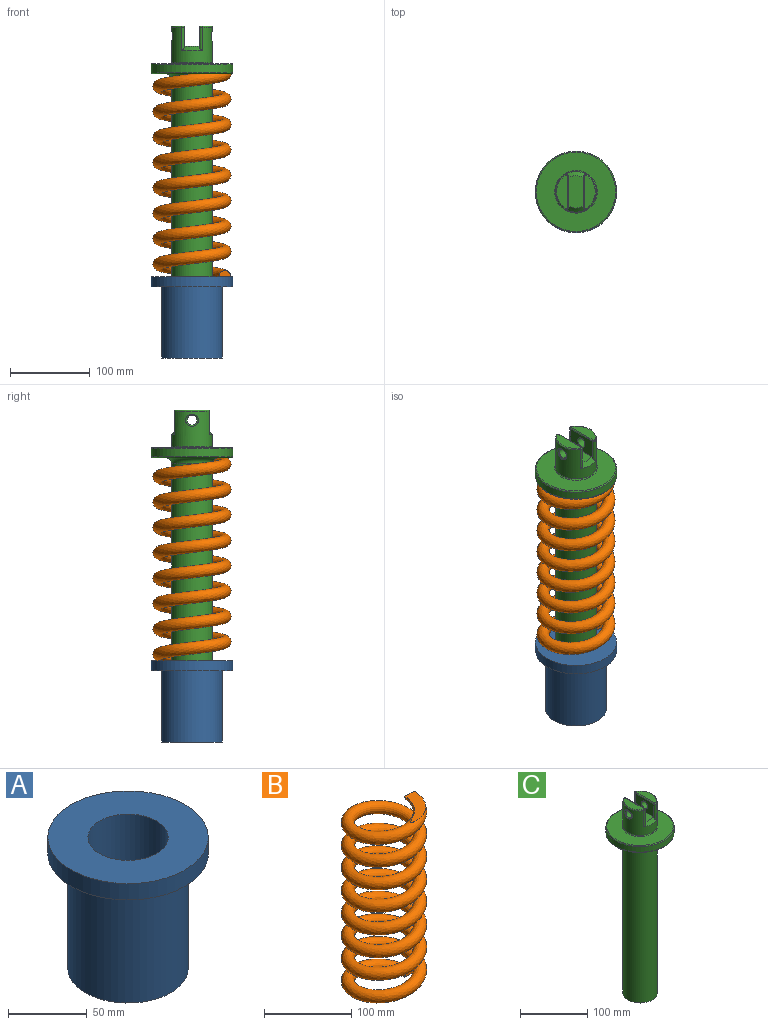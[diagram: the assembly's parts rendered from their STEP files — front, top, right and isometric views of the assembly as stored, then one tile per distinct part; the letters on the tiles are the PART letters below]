
ASSEMBLY  parts=3 mates=2
PART A: 7 faces, bbox 101.6x101.6x101.6 mm
  f0: cylinder r=25.4mm len=88.9mm, axis (0,0,1), area 14187.8mm2, adj f3,f5
  f1: cylinder r=50.8mm len=101.6mm, axis (0,0,1), area 4053.7mm2, adj f2,f3
  f2: plane 101.6x101.6mm, normal (0,0,-1), area 3547mm2, adj f1,f4
  f3: plane 101.6x101.6mm, normal (0,0,1), area 6080.5mm2, adj f0,f1
  f4: cylinder r=38.1mm len=88.9mm, axis (0,0,1), area 21281.7mm2, adj f2,f6
  f5: plane 50.8x50.8mm, normal (0,0,1), area 2026.8mm2, adj f0
  f6: plane 76.2x76.2mm, normal (0,0,-1), area 4560.4mm2, adj f4
PART B: 5 faces, bbox 99.6x99.4x271.4 mm
  f0: plane 17.4x9.78mm, normal (0,1,0), area 91.2mm2, adj f1,f3
  f1: bspline ~269.2x97.21mm, area 97858.7mm2, adj f0,f2,f3,f4
  f2: plane 17.4x9.78mm, normal (0,-1,0), area 91.2mm2, adj f1,f4
  f3: plane 46.27x43.59mm, normal (0,0,1), area 745mm2, adj f0,f1
  f4: plane 46.27x43.59mm, normal (0,0,-1), area 745.1mm2, adj f1,f2
PART C: 33 faces, bbox 110x110x351.8 mm
  f0: cylinder r=25.4mm len=50.8mm, axis (0,0,-1), area 5053.7mm2, adj f12,f13,f14,f15,f16,f17,f20,f21
  f1: plane 41.37x13.34mm, normal (0,0,1), area 409.4mm2, adj f26,f27,f28,f29
  f2: cylinder r=25.4mm len=284.48mm, axis (0,0,-1), area 45401mm2, adj f6,f7
  f3: cylinder r=50.8mm len=101.6mm, axis (0,0,-1), area 3242.9mm2, adj f31,f32
  f4: plane 99.06x99.06mm, normal (0,0,1), area 5472.4mm2, adj f30,f31
  f5: plane 99.06x99.06mm, normal (0,0,-1), area 4281.7mm2, adj f7,f32
  f6: plane 50.8x50.8mm, normal (0,0,-1), area 2026.8mm2, adj f2
  f7: torus R=33.02mm, axis (0,0,1), area 2118.5mm2, adj f2,f5
  f8: plane 41.37x13.34mm, normal (0,0,1), area 409.4mm2, adj f22,f23,f24,f25
  f9: plane 40.64x19.05mm, normal (0,0,1), area 744.8mm2, adj f10,f11,f12,f13
  f10: plane 38.86x25.46mm, normal (-1,0,0), area 812.3mm2, adj f9,f12,f13,f14,f15,f19,f28
  f11: plane 38.86x25.46mm, normal (1,0,0), area 812.3mm2, adj f9,f12,f13,f16,f17,f18,f23
  f12: cone r=20.32mm half-angle=45deg, axis (0,0,-1), area 153mm2, adj f0,f9,f10,f11,f15,f17
  f13: cone r=20.32mm half-angle=45deg, axis (0,0,-1), area 153mm2, adj f0,f9,f10,f11,f14,f16
  f14: cylinder r=2.54mm len=29.21mm, axis (0,0,-1), area 150mm2, adj f0,f10,f13,f29
  f15: cylinder r=2.54mm len=29.21mm, axis (0,0,-1), area 150mm2, adj f0,f10,f12,f26
  f16: cylinder r=2.54mm len=29.21mm, axis (0,0,-1), area 150mm2, adj f0,f11,f13,f25
  f17: cylinder r=2.54mm len=29.21mm, axis (0,0,-1), area 150mm2, adj f0,f11,f12,f22
  f18: cylinder r=6.35mm len=14.61mm, axis (1,0,0), area 558.2mm2, adj f11,f21
  f19: cylinder r=6.35mm len=14.61mm, axis (1,0,0), area 558.2mm2, adj f10,f20
  f20: bspline ~16.06x15.26mm, area 95.7mm2, adj f0,f19
  f21: bspline ~16.07x15.26mm, area 95.8mm2, adj f0,f18
  f22: torus R=1.27mm, axis (0,0,1), area 8.8mm2, adj f8,f17,f23,f24
  f23: cylinder r=1.27mm len=38.83mm, axis (0,1,0), area 77.5mm2, adj f8,f11,f22,f25
  f24: torus R=24.13mm, axis (0,0,1), area 101mm2, adj f0,f8,f22,f25
  f25: torus R=1.27mm, axis (0,0,1), area 8.8mm2, adj f8,f16,f23,f24
  f26: torus R=1.27mm, axis (0,0,1), area 8.8mm2, adj f1,f15,f27,f28
  f27: torus R=24.13mm, axis (0,0,1), area 101mm2, adj f0,f1,f26,f29
  f28: cylinder r=1.27mm len=38.83mm, axis (0,-1,0), area 77.5mm2, adj f1,f10,f26,f29
  f29: torus R=1.27mm, axis (0,0,1), area 8.8mm2, adj f1,f14,f27,f28
  f30: torus R=26.67mm, axis (0,0,1), area 324.2mm2, adj f0,f4
  f31: torus R=49.53mm, axis (0,0,1), area 631mm2, adj f3,f4
  f32: torus R=49.53mm, axis (0,0,1), area 631mm2, adj f3,f5
PLACE A t=(0.12,0.02,6.28)mm
PLACE B t=(0.12,0.02,6.28)mm
PLACE C t=(0.12,0.02,-6.42)mm
MATE planar B.f4 <-> A.f1  axis (0,0,1) through (0.12,0.02,6.28)mm
MATE cylindrical C.f0 <-> A.f0  axis (0,0,-1) through (0.12,0.02,-31.82)mm
